# Revit family: Flush_Valve_Access_Panel-Hydraulic_Flush-Whitehall-BestCare-WH2898ADA-SL_Series
name_source: partatom
category: Specialty Equipment
units: mm (PartAtom-declared; Revit-internal decimal feet)

## family parameters
Cut with Voids When Loaded = No
Host = Face
OmniClass Number = 23.30.10.27.14
OmniClass Title = Access Panels
Part Type = Normal
Room Calculation Point = No
Round Connector Dimension = Use Diameter
Shared = Yes

## types (9) — shared parameters
ADA Compliant = Yes
Assembly Code = C1030200
Default Elevation = 0"
Description = BestCare® ADA Compliant Ligature-Resistant Access Panel with Hydraulic Flush Valve
Height = 13"
Installation Type = Wall Mounted
Length = 17"
Manufacturer = Whitehall Mfg.
Product Documentation Link = https://www.whitehallmfg.com
Product Page URL = https://www.whitehallmfg.com
Pushbutton Material = Stainless Steel-Whitehall-Satin
URL = https://www.whitehallmfg.com
Width = 2 1/8"

## per-type parameters (varying)
| type | Body Material | Flush Rate | Material | Pushbutton | Type Comments |
| WH2898ADA-SL-1.28 (Toilet) | Stainless Steel-Whitehall-Powder Coated White | 1.28 GPF (4.85 LPF) | Stainless Steel-Whitehall-Powder Coated White | Yes | ADA Flush Valve Cover With 1.28 GPF Hydraulic Flush Valve (White) |
| WH2898ADA-SL-1.6 (Toilet) | Stainless Steel-Whitehall-Powder Coated White | 1.6 GPF (6 LPF) | Stainless Steel-Whitehall-Powder Coated White | Yes | ADA Flush Valve Cover With 1.6 GPF Hydraulic Flush Valve (White) |
| WH2898ADA-SL-1.28-SS (Toilet) | Stainless Steel-Whitehall-Satin | 1.28 GPF (4.85 LPF) | Stainless Steel-Whitehall-Satin | Yes | ADA Flush Valve Cover With 1.28 GPF Hydraulic Flush Valve (#4 Stn Stl Finish) |
| WH2898ADA-SL-1.6-SS (Toilet) | Stainless Steel-Whitehall-Satin | 1.6 GPF (6 LPF) | Stainless Steel-Whitehall-Satin | Yes | ADA Flush Valve Cover With 1.6 GPF Hydraulic Flush Valve (#4 Stn Stl Finish) |
| WH2898ADA-SL-0.5 (Urinal) | Stainless Steel-Whitehall-Powder Coated White | 0.5 GPF (1.89 LPF) | Stainless Steel-Whitehall-Powder Coated White | Yes | ADA Flush Valve Cover With 0.5 GPF Hydraulic Flush Valve (White) |
| WH2898ADA-SL-.125 (Urinal) | Stainless Steel-Whitehall-Powder Coated White | .125 GPF (4.85 LPF) | Stainless Steel-Whitehall-Powder Coated White | Yes | ADA Flush Valve Cover With 0.125 GPF Hydraulic Flush Valve (White) |
| WH2898ADA-SL-0.5-SS (Urinal) | Stainless Steel-Whitehall-Satin | 0.5 GPF (1.89 LPF) | Stainless Steel-Whitehall-Satin | Yes | ADA Flush Valve Cover With 0.5 GPF Hydraulic Flush Valve (#4 Stn Stl Finish) |
| WH2898ADA-SL-.125-SS (Urinal) | Stainless Steel-Whitehall-Satin | .125 GPF (4.85 LPF) | Stainless Steel-Whitehall-Satin | Yes | ADA Flush Valve Cover With 0.125 GPF Hydraulic Flush Valve (#4 Stn Stl Finish) |
| WH2898ADA-SL-BLANK | Stainless Steel-Whitehall-Satin |  | Stainless Steel-Whitehall-Satin | No | WH2898ADA-SL-BLANK Ligature Resistant Blank Access Cover and Wall Frame Only (Less Flush Valve) |

note: column(s) folded — value = type name in every type: Model

## geometry (parser evidence)
native form markers: Sweep x3
no freeform markers — native parametric forms only
